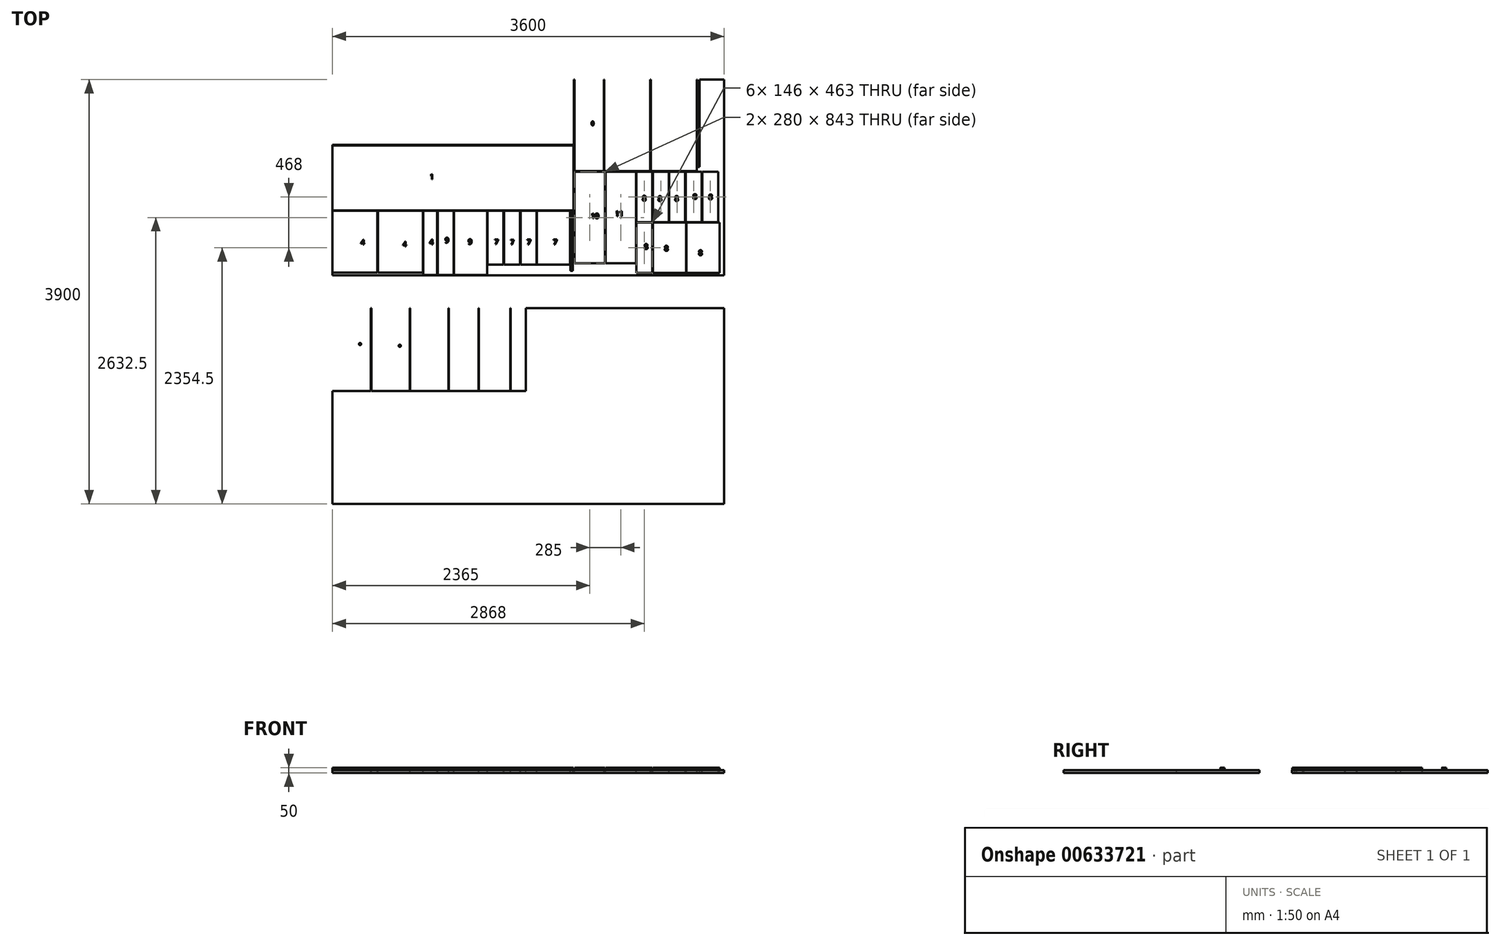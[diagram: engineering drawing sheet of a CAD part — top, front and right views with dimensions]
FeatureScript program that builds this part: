
annotation { "Feature Type Name" : "Feature", "Feature Type Description" : "" }
export const myFeature = defineFeature(function(context is Context, id is Id, definition is map)
    precondition{}
    {
        {
            var Q0;
            Q0=qCreatedBy(makeId("Top.planeOp"),FACE);
            var sketch = newSketch(context, id + "F0", { "sketchPlane" : qUnion([Q0])});
            skLineSegment(sketch, "E0.bottom", {"start": v(0, 0) * mm, "end": v(-3600, 0) * mm});
            skLineSegment(sketch, "E0.top", {"start": v(0, 1800) * mm, "end": v(-3600, 1800) * mm});
            skLineSegment(sketch, "E0.left", {"start": v(0, 0) * mm, "end": v(0, 1800) * mm});
            skLineSegment(sketch, "E0.right", {"start": v(-3600, 0) * mm, "end": v(-3600, 1800) * mm});
            skLineSegment(sketch, "E1.bottom", {"start": v(-3600, 1800) * mm, "end": v(-1380, 1800) * mm});
            skLineSegment(sketch, "E1.top", {"start": v(-3600, 1200) * mm, "end": v(-1380, 1200) * mm});
            skLineSegment(sketch, "E1.left", {"start": v(-3600, 1800) * mm, "end": v(-3600, 1200) * mm});
            skLineSegment(sketch, "E1.right", {"start": v(-1380, 1800) * mm, "end": v(-1380, 1200) * mm});
            skLineSegment(sketch, "E2.bottom", {"start": v(-3600, 1195) * mm, "end": v(-1384, 1195) * mm});
            skLineSegment(sketch, "E2.top", {"start": v(-3600, 599) * mm, "end": v(-1384, 599) * mm});
            skLineSegment(sketch, "E2.left", {"start": v(-3600, 1195) * mm, "end": v(-3600, 599) * mm});
            skLineSegment(sketch, "E2.right", {"start": v(-1384, 1195) * mm, "end": v(-1384, 599) * mm});
            skLineSegment(sketch, "E3.bottom", {"start": v(-3600, -300) * mm, "end": v(0, -300) * mm});
            skLineSegment(sketch, "E3.top", {"start": v(-3600, -2100) * mm, "end": v(0, -2100) * mm});
            skLineSegment(sketch, "E3.left", {"start": v(-3600, -300) * mm, "end": v(-3600, -2100) * mm});
            skLineSegment(sketch, "E3.right", {"start": v(0, -300) * mm, "end": v(0, -2100) * mm});
            skLineSegment(sketch, "E4.bottom", {"start": v(-3600, 594) * mm, "end": v(-3187, 594) * mm});
            skLineSegment(sketch, "E4.top", {"start": v(-3600, 28) * mm, "end": v(-3187, 28) * mm});
            skLineSegment(sketch, "E4.left", {"start": v(-3600, 594) * mm, "end": v(-3600, 28) * mm});
            skLineSegment(sketch, "E4.right", {"start": v(-3187, 594) * mm, "end": v(-3187, 28) * mm});
            skLineSegment(sketch, "E5.bottom", {"start": v(-3182, 594) * mm, "end": v(-2769, 594) * mm});
            skLineSegment(sketch, "E5.top", {"start": v(-3182, 28) * mm, "end": v(-2769, 28) * mm});
            skLineSegment(sketch, "E5.left", {"start": v(-3182, 594) * mm, "end": v(-3182, 28) * mm});
            skLineSegment(sketch, "E5.right", {"start": v(-2769, 594) * mm, "end": v(-2769, 28) * mm});
            skPoint(sketch, "E6", {"position": v(-3393.5, 28) * mm});
            skLineSegment(sketch, "E7.bottom", {"start": v(-2764, 594) * mm, "end": v(-2638, 594) * mm});
            skLineSegment(sketch, "E7.top", {"start": v(-2764, 3) * mm, "end": v(-2638, 3) * mm});
            skLineSegment(sketch, "E7.left", {"start": v(-2764, 594) * mm, "end": v(-2764, 3) * mm});
            skLineSegment(sketch, "E7.right", {"start": v(-2638, 594) * mm, "end": v(-2638, 3) * mm});
            skLineSegment(sketch, "E8.bottom", {"start": v(-2633, 594) * mm, "end": v(-2487, 594) * mm});
            skLineSegment(sketch, "E8.top", {"start": v(-2633, 3) * mm, "end": v(-2487, 3) * mm});
            skLineSegment(sketch, "E8.left", {"start": v(-2633, 594) * mm, "end": v(-2633, 3) * mm});
            skLineSegment(sketch, "E8.right", {"start": v(-2487, 594) * mm, "end": v(-2487, 3) * mm});
            skLineSegment(sketch, "E9.bottom", {"start": v(-2482, 594) * mm, "end": v(-2178, 594) * mm});
            skLineSegment(sketch, "E9.top", {"start": v(-2482, 3) * mm, "end": v(-2178, 3) * mm});
            skLineSegment(sketch, "E9.left", {"start": v(-2482, 594) * mm, "end": v(-2482, 3) * mm});
            skLineSegment(sketch, "E9.right", {"start": v(-2178, 594) * mm, "end": v(-2178, 3) * mm});
            skLineSegment(sketch, "E10.bottom", {"start": v(-2173, 594) * mm, "end": v(-2027, 594) * mm});
            skLineSegment(sketch, "E10.top", {"start": v(-2173, 99) * mm, "end": v(-2027, 99) * mm});
            skLineSegment(sketch, "E10.left", {"start": v(-2173, 594) * mm, "end": v(-2173, 99) * mm});
            skLineSegment(sketch, "E10.right", {"start": v(-2027, 594) * mm, "end": v(-2027, 99) * mm});
            skLineSegment(sketch, "E11.bottom", {"start": v(-2022, 594) * mm, "end": v(-1876, 594) * mm});
            skLineSegment(sketch, "E11.top", {"start": v(-2022, 99) * mm, "end": v(-1876, 99) * mm});
            skLineSegment(sketch, "E11.left", {"start": v(-2022, 594) * mm, "end": v(-2022, 99) * mm});
            skLineSegment(sketch, "E11.right", {"start": v(-1876, 594) * mm, "end": v(-1876, 99) * mm});
            skLineSegment(sketch, "E12.bottom", {"start": v(-1871, 594) * mm, "end": v(-1725, 594) * mm});
            skLineSegment(sketch, "E12.top", {"start": v(-1871, 99) * mm, "end": v(-1725, 99) * mm});
            skLineSegment(sketch, "E12.left", {"start": v(-1871, 594) * mm, "end": v(-1871, 99) * mm});
            skLineSegment(sketch, "E12.right", {"start": v(-1725, 594) * mm, "end": v(-1725, 99) * mm});
            skLineSegment(sketch, "E13", {"start": v(-1380, 1800) * mm, "end": v(-1380, 0) * mm, "construction": true});
            skLineSegment(sketch, "E14.bottom", {"start": v(-1720, 594) * mm, "end": v(-1416, 594) * mm});
            skLineSegment(sketch, "E14.top", {"start": v(-1720, 99) * mm, "end": v(-1416, 99) * mm});
            skLineSegment(sketch, "E14.left", {"start": v(-1720, 594) * mm, "end": v(-1720, 99) * mm});
            skLineSegment(sketch, "E14.right", {"start": v(-1416, 594) * mm, "end": v(-1416, 99) * mm});
            skText(sketch, "E15", { "text": "7", "fontName": "OpenSans-Regular.ttf"});
            skText(sketch, "E16", { "text": "7", "fontName": "OpenSans-Regular.ttf"});
            skText(sketch, "E17", { "text": "7", "fontName": "OpenSans-Regular.ttf"});
            skText(sketch, "E18", { "text": "7", "fontName": "OpenSans-Regular.ttf"});
            skText(sketch, "E19", { "text": "9", "fontName": "OpenSans-Regular.ttf"});
            skText(sketch, "E20", { "text": "9", "fontName": "OpenSans-Regular.ttf"});
            skText(sketch, "E21", { "text": "4", "fontName": "OpenSans-Regular.ttf"});
            skText(sketch, "E22", { "text": "4", "fontName": "OpenSans-Regular.ttf"});
            skText(sketch, "E23", { "text": "4", "fontName": "OpenSans-Regular.ttf"});
            skText(sketch, "E24", { "text": "1", "fontName": "OpenSans-Regular.ttf"});
            skText(sketch, "E25", { "text": "1", "fontName": "OpenSans-Regular.ttf"});
            skLineSegment(sketch, "E26.bottom", {"start": v(-3600, -300) * mm, "end": v(-3247.5, -300) * mm});
            skLineSegment(sketch, "E26.top", {"start": v(-3600, -1061) * mm, "end": v(-3247.5, -1061) * mm});
            skLineSegment(sketch, "E26.left", {"start": v(-3600, -300) * mm, "end": v(-3600, -1061) * mm});
            skLineSegment(sketch, "E26.right", {"start": v(-3247.5, -300) * mm, "end": v(-3247.5, -1061) * mm});
            skLineSegment(sketch, "E27.bottom", {"start": v(-3242.5, -300) * mm, "end": v(-2890, -300) * mm});
            skLineSegment(sketch, "E27.top", {"start": v(-3242.5, -1061) * mm, "end": v(-2890, -1061) * mm});
            skLineSegment(sketch, "E27.left", {"start": v(-3242.5, -300) * mm, "end": v(-3242.5, -1061) * mm});
            skLineSegment(sketch, "E27.right", {"start": v(-2890, -300) * mm, "end": v(-2890, -1061) * mm});
            skLineSegment(sketch, "E28.bottom", {"start": v(-2885, -300) * mm, "end": v(-2534, -300) * mm});
            skLineSegment(sketch, "E28.top", {"start": v(-2885, -1061) * mm, "end": v(-2534, -1061) * mm});
            skLineSegment(sketch, "E28.left", {"start": v(-2885, -300) * mm, "end": v(-2885, -1061) * mm});
            skLineSegment(sketch, "E28.right", {"start": v(-2534, -300) * mm, "end": v(-2534, -1061) * mm});
            skLineSegment(sketch, "E29.bottom", {"start": v(-2253, -300) * mm, "end": v(-1965, -300) * mm});
            skLineSegment(sketch, "E29.top", {"start": v(-2253, -1061) * mm, "end": v(-1965, -1061) * mm});
            skLineSegment(sketch, "E29.left", {"start": v(-2253, -300) * mm, "end": v(-2253, -1061) * mm});
            skLineSegment(sketch, "E29.right", {"start": v(-1965, -300) * mm, "end": v(-1965, -1061) * mm});
            skLineSegment(sketch, "E30.bottom", {"start": v(-2529, -300) * mm, "end": v(-2258, -300) * mm});
            skLineSegment(sketch, "E30.top", {"start": v(-2529, -1061) * mm, "end": v(-2258, -1061) * mm});
            skLineSegment(sketch, "E30.left", {"start": v(-2529, -300) * mm, "end": v(-2529, -1061) * mm});
            skLineSegment(sketch, "E30.right", {"start": v(-2258, -300) * mm, "end": v(-2258, -1061) * mm});
            skLineSegment(sketch, "E31.bottom", {"start": v(-1960, -300) * mm, "end": v(-1821, -300) * mm});
            skLineSegment(sketch, "E31.top", {"start": v(-1960, -1061) * mm, "end": v(-1821, -1061) * mm});
            skLineSegment(sketch, "E31.left", {"start": v(-1960, -300) * mm, "end": v(-1960, -1061) * mm});
            skLineSegment(sketch, "E31.right", {"start": v(-1821, -300) * mm, "end": v(-1821, -1061) * mm});
            skText(sketch, "E32", { "text": "6", "fontName": "OpenSans-Regular.ttf"});
            skText(sketch, "E33", { "text": "6", "fontName": "OpenSans-Regular.ttf"});
            skText(sketch, "E34", { "text": "5", "fontName": "OpenSans-Regular.ttf"});
            skText(sketch, "E35", { "text": "5", "fontName": "OpenSans-Regular.ttf"});
            skText(sketch, "E36", { "text": "7", "fontName": "OpenSans-Regular.ttf"});
            skText(sketch, "E37", { "text": "3", "fontName": "OpenSans-Regular.ttf"});
            skLineSegment(sketch, "E38.bottom", {"start": v(-1375, 954) * mm, "end": v(-1095, 954) * mm});
            skLineSegment(sketch, "E38.top", {"start": v(-1375, 111) * mm, "end": v(-1095, 111) * mm});
            skLineSegment(sketch, "E38.left", {"start": v(-1375, 954) * mm, "end": v(-1375, 111) * mm});
            skLineSegment(sketch, "E38.right", {"start": v(-1095, 954) * mm, "end": v(-1095, 111) * mm});
            skLineSegment(sketch, "E39.bottom", {"start": v(-673.5, 1800) * mm, "end": v(-251, 1800) * mm});
            skLineSegment(sketch, "E39.top", {"start": v(-673.5, 959) * mm, "end": v(-251, 959) * mm});
            skLineSegment(sketch, "E39.left", {"start": v(-673.5, 1800) * mm, "end": v(-673.5, 959) * mm});
            skLineSegment(sketch, "E39.right", {"start": v(-251, 1800) * mm, "end": v(-251, 959) * mm});
            skLineSegment(sketch, "E40.bottom", {"start": v(-1375, 1800) * mm, "end": v(-1106, 1800) * mm});
            skLineSegment(sketch, "E40.top", {"start": v(-1375, 959) * mm, "end": v(-1106, 959) * mm});
            skLineSegment(sketch, "E40.left", {"start": v(-1375, 1800) * mm, "end": v(-1375, 959) * mm});
            skLineSegment(sketch, "E40.right", {"start": v(-1106, 1800) * mm, "end": v(-1106, 959) * mm});
            skLineSegment(sketch, "E41.bottom", {"start": v(-1101, 1800) * mm, "end": v(-678.5, 1800) * mm});
            skLineSegment(sketch, "E41.top", {"start": v(-1101, 959) * mm, "end": v(-678.5, 959) * mm});
            skLineSegment(sketch, "E41.left", {"start": v(-1101, 1800) * mm, "end": v(-1101, 959) * mm});
            skLineSegment(sketch, "E41.right", {"start": v(-678.5, 1800) * mm, "end": v(-678.5, 959) * mm});
            skLineSegment(sketch, "E42.bottom", {"start": v(-246, 1800) * mm, "end": v(-226, 1800) * mm});
            skLineSegment(sketch, "E42.top", {"start": v(-246, 998) * mm, "end": v(-226, 998) * mm});
            skLineSegment(sketch, "E42.left", {"start": v(-246, 1800) * mm, "end": v(-246, 998) * mm});
            skLineSegment(sketch, "E42.right", {"start": v(-226, 1800) * mm, "end": v(-226, 998) * mm});
            skLineSegment(sketch, "E43", {"start": v(-1375, 959) * mm, "end": v(0, 959) * mm, "construction": true});
            skText(sketch, "E44", { "text": "10", "fontName": "OpenSans-Regular.ttf"});
            skText(sketch, "E45", { "text": "11", "fontName": "OpenSans-Regular.ttf"});
            skText(sketch, "E46", { "text": "11", "fontName": "OpenSans-Regular.ttf"});
            skText(sketch, "E47", { "text": "10", "fontName": "OpenSans-Regular.ttf"});
            skLineSegment(sketch, "E48.bottom", {"start": v(-1090, 954) * mm, "end": v(-810, 954) * mm});
            skLineSegment(sketch, "E48.top", {"start": v(-1090, 111) * mm, "end": v(-810, 111) * mm});
            skLineSegment(sketch, "E48.left", {"start": v(-1090, 954) * mm, "end": v(-1090, 111) * mm});
            skLineSegment(sketch, "E48.right", {"start": v(-810, 954) * mm, "end": v(-810, 111) * mm});
            skText(sketch, "E49", { "text": "11", "fontName": "OpenSans-Regular.ttf"});
            skLineSegment(sketch, "E50.bottom", {"start": v(-805, 954) * mm, "end": v(-659, 954) * mm});
            skLineSegment(sketch, "E50.top", {"start": v(-805, 491) * mm, "end": v(-659, 491) * mm});
            skLineSegment(sketch, "E50.left", {"start": v(-805, 954) * mm, "end": v(-805, 491) * mm});
            skLineSegment(sketch, "E50.right", {"start": v(-659, 954) * mm, "end": v(-659, 491) * mm});
            skLineSegment(sketch, "E51.bottom", {"start": v(-654, 954) * mm, "end": v(-508, 954) * mm});
            skLineSegment(sketch, "E51.top", {"start": v(-654, 491) * mm, "end": v(-508, 491) * mm});
            skLineSegment(sketch, "E51.left", {"start": v(-654, 954) * mm, "end": v(-654, 491) * mm});
            skLineSegment(sketch, "E51.right", {"start": v(-508, 954) * mm, "end": v(-508, 491) * mm});
            skLineSegment(sketch, "E52.bottom", {"start": v(-503, 954) * mm, "end": v(-357, 954) * mm});
            skLineSegment(sketch, "E52.top", {"start": v(-503, 491) * mm, "end": v(-357, 491) * mm});
            skLineSegment(sketch, "E52.left", {"start": v(-503, 954) * mm, "end": v(-503, 491) * mm});
            skLineSegment(sketch, "E52.right", {"start": v(-357, 954) * mm, "end": v(-357, 491) * mm});
            skLineSegment(sketch, "E53.bottom", {"start": v(-352, 954) * mm, "end": v(-206, 954) * mm});
            skLineSegment(sketch, "E53.top", {"start": v(-352, 491) * mm, "end": v(-206, 491) * mm});
            skLineSegment(sketch, "E53.left", {"start": v(-352, 954) * mm, "end": v(-352, 491) * mm});
            skLineSegment(sketch, "E53.right", {"start": v(-206, 954) * mm, "end": v(-206, 491) * mm});
            skLineSegment(sketch, "E54.bottom", {"start": v(-201, 954) * mm, "end": v(-55, 954) * mm});
            skLineSegment(sketch, "E54.top", {"start": v(-201, 491) * mm, "end": v(-55, 491) * mm});
            skLineSegment(sketch, "E54.left", {"start": v(-201, 954) * mm, "end": v(-201, 491) * mm});
            skLineSegment(sketch, "E54.right", {"start": v(-55, 954) * mm, "end": v(-55, 491) * mm});
            skLineSegment(sketch, "E55.bottom", {"start": v(-805, 486) * mm, "end": v(-659, 486) * mm});
            skLineSegment(sketch, "E55.top", {"start": v(-805, 23) * mm, "end": v(-659, 23) * mm});
            skLineSegment(sketch, "E55.left", {"start": v(-805, 486) * mm, "end": v(-805, 23) * mm});
            skLineSegment(sketch, "E55.right", {"start": v(-659, 486) * mm, "end": v(-659, 23) * mm});
            skLineSegment(sketch, "E56.bottom", {"start": v(-654, 486) * mm, "end": v(-350, 486) * mm});
            skLineSegment(sketch, "E56.top", {"start": v(-654, 23) * mm, "end": v(-350, 23) * mm});
            skLineSegment(sketch, "E56.left", {"start": v(-654, 486) * mm, "end": v(-654, 23) * mm});
            skLineSegment(sketch, "E56.right", {"start": v(-350, 486) * mm, "end": v(-350, 23) * mm});
            skLineSegment(sketch, "E57.bottom", {"start": v(-1411, 594) * mm, "end": v(-1391, 594) * mm});
            skLineSegment(sketch, "E57.top", {"start": v(-1411, 42) * mm, "end": v(-1391, 42) * mm});
            skLineSegment(sketch, "E57.left", {"start": v(-1411, 594) * mm, "end": v(-1411, 42) * mm});
            skLineSegment(sketch, "E57.right", {"start": v(-1391, 594) * mm, "end": v(-1391, 42) * mm});
            skText(sketch, "E58", { "text": "8", "fontName": "OpenSans-Regular.ttf"});
            skText(sketch, "E59", { "text": "8", "fontName": "OpenSans-Regular.ttf"});
            skText(sketch, "E60", { "text": "8", "fontName": "OpenSans-Regular.ttf"});
            skText(sketch, "E61", { "text": "8", "fontName": "OpenSans-Regular.ttf"});
            skText(sketch, "E62", { "text": "8", "fontName": "OpenSans-Regular.ttf"});
            skText(sketch, "E63", { "text": "8", "fontName": "OpenSans-Regular.ttf"});
            skText(sketch, "E64", { "text": "8", "fontName": "OpenSans-Regular.ttf"});
            skLineSegment(sketch, "E65.bottom", {"start": v(-345, 486) * mm, "end": v(-41, 486) * mm});
            skLineSegment(sketch, "E65.top", {"start": v(-345, 23) * mm, "end": v(-41, 23) * mm});
            skLineSegment(sketch, "E65.left", {"start": v(-345, 486) * mm, "end": v(-345, 23) * mm});
            skLineSegment(sketch, "E65.right", {"start": v(-41, 486) * mm, "end": v(-41, 23) * mm});
            skText(sketch, "E66", { "text": "8", "fontName": "OpenSans-Regular.ttf"});
            const initialGuessF0  = {"E15": [-2.10921, 0.2869, 1, 0, 0.04638], "E16": [-1.965, 0.28355, 1, 0, 0.04638], "E17": [-1.8111, 0.2845, 1, 0, 0.04638], "E18": [-1.5711, 0.2845, 1, 0, 0.04638], "E19": [-2.35296, 0.28738, 1, 0, 0.04638], "E20": [-2.56596, 0.3013, 1, 0, 0.04638], "E21": [-2.709, 0.2855, 1, 0, 0.04638], "E22": [-2.9545, 0.26558, 1, 0, 0.04638], "E23": [-3.34023, 0.2825, 1, 0, 0.04638], "E24": [-2.7, 1.47, 1, 0, 0.04638], "E25": [-2.70346, 0.885, 1, 0, 0.04638], "E32": [-3.3649, -0.6445, 1, 0, 0.04638], "E33": [-3.00034, -0.66125, 1, 0, 0.04638], "E34": [-2.6205, -0.674, 1, 0, 0.04638], "E35": [-2.326, -0.6861, 1, 0, 0.04638], "E36": [-1.90976, -0.67968, 1, 0, 0.04638], "E37": [-2.11362, -0.68108, 1, 0, 0.04638], "E44": [-1.26293, 1.37555, 1, 0, 0.04638], "E45": [-0.88838, 1.39262, 1, 0, 0.04638], "E46": [-0.4975, 1.35498, 1, 0, 0.04638], "E47": [-1.22373, 0.52433, 1, 0, 0.04638], "E49": [-1.0003, 0.54532, 1, 0, 0.04638], "E58": [-0.549, 0.22673, 1, 0, 0.04638], "E59": [-0.75213, 0.68705, 1, 0, 0.04638], "E60": [-0.60792, 0.6837, 1, 0, 0.04638], "E61": [-0.454, 0.68466, 1, 0, 0.04638], "E62": [-0.28651, 0.7023, 1, 0, 0.04638], "E63": [-0.1423, 0.69897, 1, 0, 0.04638], "E64": [-0.735, 0.24273, 1, 0, 0.04638], "E66": [-0.2351, 0.18613, 1, 0, 0.04638]};
            skSetInitialGuess(sketch, initialGuessF0);
            skSolve(sketch);
        }
        {
            var Q0;
            Q0=makeQuery(id+"F0.imprint","IMPRINT",FACE,{"disambiguationData":[TD([[makeQuery(id+"F0.imprint","IMPRINT",EDGE,{"derivedFrom":sQuery(id+"F0.wireOp",EDGE,"E4.bottom")}),-1.0]])]});
            var Q1;
            Q1=makeQuery(id+"F0.imprint","IMPRINT",FACE,{"disambiguationData":[TD([[makeQuery(id+"F0.imprint","IMPRINT",EDGE,{"derivedFrom":sQuery(id+"F0.wireOp",EDGE,"E5.bottom")}),-1.0]])]});
            var Q2;
            Q2=makeQuery(id+"F0.imprint","IMPRINT",FACE,{"disambiguationData":[TD([[makeQuery(id+"F0.imprint","IMPRINT",EDGE,{"derivedFrom":sQuery(id+"F0.wireOp",EDGE,"E7.bottom")}),-1.0]])]});
            var Q3;
            Q3=makeQuery(id+"F0.imprint","IMPRINT",FACE,{"disambiguationData":[TD([[makeQuery(id+"F0.imprint","IMPRINT",EDGE,{"derivedFrom":sQuery(id+"F0.wireOp",EDGE,"E8.bottom")}),-1.0]])]});
            var Q4;
            Q4=makeQuery(id+"F0.imprint","IMPRINT",FACE,{"disambiguationData":[TD([[makeQuery(id+"F0.imprint","IMPRINT",EDGE,{"derivedFrom":sQuery(id+"F0.wireOp",EDGE,"E9.bottom")}),-1.0]])]});
            var Q5;
            Q5=makeQuery(id+"F0.imprint","IMPRINT",FACE,{"disambiguationData":[TD([[makeQuery(id+"F0.imprint","IMPRINT",EDGE,{"derivedFrom":sQuery(id+"F0.wireOp",EDGE,"E10.bottom")}),-1.0]])]});
            var Q6;
            Q6=makeQuery(id+"F0.imprint","IMPRINT",FACE,{"disambiguationData":[TD([[makeQuery(id+"F0.imprint","IMPRINT",EDGE,{"derivedFrom":sQuery(id+"F0.wireOp",EDGE,"E11.bottom")}),-1.0]])]});
            var Q7;
            Q7=makeQuery(id+"F0.imprint","IMPRINT",FACE,{"disambiguationData":[TD([[makeQuery(id+"F0.imprint","IMPRINT",EDGE,{"derivedFrom":sQuery(id+"F0.wireOp",EDGE,"E12.bottom")}),-1.0]])]});
            var Q8;
            Q8=makeQuery(id+"F0.imprint","IMPRINT",FACE,{"disambiguationData":[TD([[makeQuery(id+"F0.imprint","IMPRINT",EDGE,{"derivedFrom":sQuery(id+"F0.wireOp",EDGE,"E14.bottom")}),-1.0]])]});
            var Q9;
            Q9=makeQuery(id+"F0.imprint","IMPRINT",FACE,{"disambiguationData":[TD([[makeQuery(id+"F0.imprint","IMPRINT",EDGE,{"derivedFrom":sQuery(id+"F0.wireOp",EDGE,"E57.bottom")}),-1.0]])]});
            var Q10;
            Q10=makeQuery(id+"F0.imprint","IMPRINT",FACE,{"disambiguationData":[TD([[makeQuery(id+"F0.imprint","IMPRINT",EDGE,{"derivedFrom":sQuery(id+"F0.wireOp",EDGE,"E38.bottom")}),-1.0]])]});
            var Q11;
            Q11=makeQuery(id+"F0.imprint","IMPRINT",FACE,{"disambiguationData":[TD([[makeQuery(id+"F0.imprint","IMPRINT",EDGE,{"derivedFrom":sQuery(id+"F0.wireOp",EDGE,"E47.sketch_text.stroke-17")}),1.0]])]});
            var Q12;
            Q12=makeQuery(id+"F0.imprint","IMPRINT",FACE,{"disambiguationData":[TD([[makeQuery(id+"F0.imprint","IMPRINT",EDGE,{"derivedFrom":sQuery(id+"F0.wireOp",EDGE,"E48.bottom")}),-1.0]])]});
            var Q13;
            Q13=makeQuery(id+"F0.imprint","IMPRINT",FACE,{"disambiguationData":[TD([[makeQuery(id+"F0.imprint","IMPRINT",EDGE,{"derivedFrom":sQuery(id+"F0.wireOp",EDGE,"E2.bottom")}),-1.0]])]});
            var Q14;
            Q14=makeQuery(id+"F0.imprint","IMPRINT",FACE,{"disambiguationData":[TD([[makeQuery(id+"F0.imprint","IMPRINT",EDGE,{"derivedFrom":sQuery(id+"F0.wireOp",EDGE,"E21.sketch_text.stroke-11")}),1.0]])]});
            var Q15;
            Q15=makeQuery(id+"F0.imprint","IMPRINT",FACE,{"disambiguationData":[TD([[makeQuery(id+"F0.imprint","IMPRINT",EDGE,{"derivedFrom":sQuery(id+"F0.wireOp",EDGE,"E20.sketch_text.stroke-16")}),1.0]])]});
            var Q16;
            Q16=makeQuery(id+"F0.imprint","IMPRINT",FACE,{"disambiguationData":[TD([[makeQuery(id+"F0.imprint","IMPRINT",EDGE,{"derivedFrom":sQuery(id+"F0.wireOp",EDGE,"E19.sketch_text.stroke-16")}),1.0]])]});
            var Q17;
            Q17=makeQuery(id+"F0.imprint","IMPRINT",FACE,{"disambiguationData":[TD([[makeQuery(id+"F0.imprint","IMPRINT",EDGE,{"derivedFrom":sQuery(id+"F0.wireOp",EDGE,"E22.sketch_text.stroke-11")}),1.0]])]});
            var Q18;
            Q18=makeQuery(id+"F0.imprint","IMPRINT",FACE,{"disambiguationData":[TD([[makeQuery(id+"F0.imprint","IMPRINT",EDGE,{"derivedFrom":sQuery(id+"F0.wireOp",EDGE,"E23.sketch_text.stroke-11")}),1.0]])]});
            var Q19;
            Q19=makeQuery(id+"F0.imprint","IMPRINT",FACE,{"disambiguationData":[TD([[makeQuery(id+"F0.imprint","IMPRINT",EDGE,{"derivedFrom":sQuery(id+"F0.wireOp",EDGE,"E55.bottom")}),-1.0]])]});
            var Q20;
            Q20=makeQuery(id+"F0.imprint","IMPRINT",FACE,{"disambiguationData":[TD([[makeQuery(id+"F0.imprint","IMPRINT",EDGE,{"derivedFrom":sQuery(id+"F0.wireOp",EDGE,"E64.sketch_text.stroke-15")}),1.0]])]});
            var Q21;
            Q21=makeQuery(id+"F0.imprint","IMPRINT",FACE,{"disambiguationData":[TD([[makeQuery(id+"F0.imprint","IMPRINT",EDGE,{"derivedFrom":sQuery(id+"F0.wireOp",EDGE,"E64.sketch_text.stroke-23")}),1.0]])]});
            var Q22;
            Q22=makeQuery(id+"F0.imprint","IMPRINT",FACE,{"disambiguationData":[TD([[makeQuery(id+"F0.imprint","IMPRINT",EDGE,{"derivedFrom":sQuery(id+"F0.wireOp",EDGE,"E56.bottom")}),-1.0]])]});
            var Q23;
            Q23=makeQuery(id+"F0.imprint","IMPRINT",FACE,{"disambiguationData":[TD([[makeQuery(id+"F0.imprint","IMPRINT",EDGE,{"derivedFrom":sQuery(id+"F0.wireOp",EDGE,"E58.sketch_text.stroke-15")}),1.0]])]});
            var Q24;
            Q24=makeQuery(id+"F0.imprint","IMPRINT",FACE,{"disambiguationData":[TD([[makeQuery(id+"F0.imprint","IMPRINT",EDGE,{"derivedFrom":sQuery(id+"F0.wireOp",EDGE,"E58.sketch_text.stroke-23")}),1.0]])]});
            var Q25;
            Q25=makeQuery(id+"F0.imprint","IMPRINT",FACE,{"disambiguationData":[TD([[makeQuery(id+"F0.imprint","IMPRINT",EDGE,{"derivedFrom":sQuery(id+"F0.wireOp",EDGE,"E65.bottom")}),-1.0]])]});
            var Q26;
            Q26=makeQuery(id+"F0.imprint","IMPRINT",FACE,{"disambiguationData":[TD([[makeQuery(id+"F0.imprint","IMPRINT",EDGE,{"derivedFrom":sQuery(id+"F0.wireOp",EDGE,"E66.sketch_text.stroke-15")}),1.0]])]});
            var Q27;
            Q27=makeQuery(id+"F0.imprint","IMPRINT",FACE,{"disambiguationData":[TD([[makeQuery(id+"F0.imprint","IMPRINT",EDGE,{"derivedFrom":sQuery(id+"F0.wireOp",EDGE,"E66.sketch_text.stroke-23")}),1.0]])]});
            var Q28;
            Q28=makeQuery(id+"F0.imprint","IMPRINT",FACE,{"disambiguationData":[TD([[makeQuery(id+"F0.imprint","IMPRINT",EDGE,{"derivedFrom":sQuery(id+"F0.wireOp",EDGE,"E54.bottom")}),-1.0]])]});
            var Q29;
            Q29=makeQuery(id+"F0.imprint","IMPRINT",FACE,{"disambiguationData":[TD([[makeQuery(id+"F0.imprint","IMPRINT",EDGE,{"derivedFrom":sQuery(id+"F0.wireOp",EDGE,"E53.bottom")}),-1.0]])]});
            var Q30;
            Q30=makeQuery(id+"F0.imprint","IMPRINT",FACE,{"disambiguationData":[TD([[makeQuery(id+"F0.imprint","IMPRINT",EDGE,{"derivedFrom":sQuery(id+"F0.wireOp",EDGE,"E52.bottom")}),-1.0]])]});
            var Q31;
            Q31=makeQuery(id+"F0.imprint","IMPRINT",FACE,{"disambiguationData":[TD([[makeQuery(id+"F0.imprint","IMPRINT",EDGE,{"derivedFrom":sQuery(id+"F0.wireOp",EDGE,"E51.bottom")}),-1.0]])]});
            var Q32;
            Q32=makeQuery(id+"F0.imprint","IMPRINT",FACE,{"disambiguationData":[TD([[makeQuery(id+"F0.imprint","IMPRINT",EDGE,{"derivedFrom":sQuery(id+"F0.wireOp",EDGE,"E50.bottom")}),-1.0]])]});
            var Q33;
            Q33=makeQuery(id+"F0.imprint","IMPRINT",FACE,{"disambiguationData":[TD([[makeQuery(id+"F0.imprint","IMPRINT",EDGE,{"derivedFrom":sQuery(id+"F0.wireOp",EDGE,"E59.sketch_text.stroke-23")}),1.0]])]});
            var Q34;
            Q34=makeQuery(id+"F0.imprint","IMPRINT",FACE,{"disambiguationData":[TD([[makeQuery(id+"F0.imprint","IMPRINT",EDGE,{"derivedFrom":sQuery(id+"F0.wireOp",EDGE,"E59.sketch_text.stroke-15")}),1.0]])]});
            var Q35;
            Q35=makeQuery(id+"F0.imprint","IMPRINT",FACE,{"disambiguationData":[TD([[makeQuery(id+"F0.imprint","IMPRINT",EDGE,{"derivedFrom":sQuery(id+"F0.wireOp",EDGE,"E60.sketch_text.stroke-15")}),1.0]])]});
            var Q36;
            Q36=makeQuery(id+"F0.imprint","IMPRINT",FACE,{"disambiguationData":[TD([[makeQuery(id+"F0.imprint","IMPRINT",EDGE,{"derivedFrom":sQuery(id+"F0.wireOp",EDGE,"E60.sketch_text.stroke-23")}),1.0]])]});
            var Q37;
            Q37=makeQuery(id+"F0.imprint","IMPRINT",FACE,{"disambiguationData":[TD([[makeQuery(id+"F0.imprint","IMPRINT",EDGE,{"derivedFrom":sQuery(id+"F0.wireOp",EDGE,"E61.sketch_text.stroke-15")}),1.0]])]});
            var Q38;
            Q38=makeQuery(id+"F0.imprint","IMPRINT",FACE,{"disambiguationData":[TD([[makeQuery(id+"F0.imprint","IMPRINT",EDGE,{"derivedFrom":sQuery(id+"F0.wireOp",EDGE,"E61.sketch_text.stroke-23")}),1.0]])]});
            var Q39;
            Q39=makeQuery(id+"F0.imprint","IMPRINT",FACE,{"disambiguationData":[TD([[makeQuery(id+"F0.imprint","IMPRINT",EDGE,{"derivedFrom":sQuery(id+"F0.wireOp",EDGE,"E62.sketch_text.stroke-15")}),1.0]])]});
            var Q40;
            Q40=makeQuery(id+"F0.imprint","IMPRINT",FACE,{"disambiguationData":[TD([[makeQuery(id+"F0.imprint","IMPRINT",EDGE,{"derivedFrom":sQuery(id+"F0.wireOp",EDGE,"E62.sketch_text.stroke-23")}),1.0]])]});
            var Q41;
            Q41=makeQuery(id+"F0.imprint","IMPRINT",FACE,{"disambiguationData":[TD([[makeQuery(id+"F0.imprint","IMPRINT",EDGE,{"derivedFrom":sQuery(id+"F0.wireOp",EDGE,"E63.sketch_text.stroke-15")}),1.0]])]});
            var Q42;
            Q42=makeQuery(id+"F0.imprint","IMPRINT",FACE,{"disambiguationData":[TD([[makeQuery(id+"F0.imprint","IMPRINT",EDGE,{"derivedFrom":sQuery(id+"F0.wireOp",EDGE,"E63.sketch_text.stroke-23")}),1.0]])]});
            var Q43;
            Q43=makeQuery(id+"F0.imprint","IMPRINT",FACE,{"disambiguationData":[TD([[makeQuery(id+"F0.imprint","IMPRINT",EDGE,{"derivedFrom":sQuery(id+"F0.wireOp",EDGE,"E40.bottom")}),-1.0]])]});
            var Q44;
            Q44=makeQuery(id+"F0.imprint","IMPRINT",FACE,{"disambiguationData":[TD([[makeQuery(id+"F0.imprint","IMPRINT",EDGE,{"derivedFrom":sQuery(id+"F0.wireOp",EDGE,"E41.bottom")}),-1.0]])]});
            var Q45;
            Q45=makeQuery(id+"F0.imprint","IMPRINT",FACE,{"disambiguationData":[TD([[makeQuery(id+"F0.imprint","IMPRINT",EDGE,{"derivedFrom":sQuery(id+"F0.wireOp",EDGE,"E1.bottom")}),-1.0]])]});
            var Q46;
            Q46=makeQuery(id+"F0.imprint","IMPRINT",FACE,{"disambiguationData":[TD([[makeQuery(id+"F0.imprint","IMPRINT",EDGE,{"derivedFrom":sQuery(id+"F0.wireOp",EDGE,"E39.bottom")}),-1.0]])]});
            var Q47;
            Q47=makeQuery(id+"F0.imprint","IMPRINT",FACE,{"disambiguationData":[TD([[makeQuery(id+"F0.imprint","IMPRINT",EDGE,{"derivedFrom":sQuery(id+"F0.wireOp",EDGE,"E42.bottom")}),-1.0]])]});
            var Q48;
            Q48=makeQuery(id+"F0.imprint","IMPRINT",FACE,{"disambiguationData":[TD([[makeQuery(id+"F0.imprint","IMPRINT",EDGE,{"derivedFrom":sQuery(id+"F0.wireOp",EDGE,"E44.sketch_text.stroke-17")}),1.0]])]});
            var Q49;
            Q49=makeQuery(id+"F0.imprint","IMPRINT",FACE,{"disambiguationData":[TD([[makeQuery(id+"F0.imprint","IMPRINT",EDGE,{"derivedFrom":sQuery(id+"F0.wireOp",EDGE,"E26.bottom")}),-1.0]])]});
            var Q50;
            Q50=makeQuery(id+"F0.imprint","IMPRINT",FACE,{"disambiguationData":[TD([[makeQuery(id+"F0.imprint","IMPRINT",EDGE,{"derivedFrom":sQuery(id+"F0.wireOp",EDGE,"E27.bottom")}),-1.0]])]});
            var Q51;
            Q51=makeQuery(id+"F0.imprint","IMPRINT",FACE,{"disambiguationData":[TD([[makeQuery(id+"F0.imprint","IMPRINT",EDGE,{"derivedFrom":sQuery(id+"F0.wireOp",EDGE,"E28.bottom")}),-1.0]])]});
            var Q52;
            Q52=makeQuery(id+"F0.imprint","IMPRINT",FACE,{"disambiguationData":[TD([[makeQuery(id+"F0.imprint","IMPRINT",EDGE,{"derivedFrom":sQuery(id+"F0.wireOp",EDGE,"E30.bottom")}),-1.0]])]});
            var Q53;
            Q53=makeQuery(id+"F0.imprint","IMPRINT",FACE,{"disambiguationData":[TD([[makeQuery(id+"F0.imprint","IMPRINT",EDGE,{"derivedFrom":sQuery(id+"F0.wireOp",EDGE,"E29.bottom")}),-1.0]])]});
            var Q54;
            Q54=makeQuery(id+"F0.imprint","IMPRINT",FACE,{"disambiguationData":[TD([[makeQuery(id+"F0.imprint","IMPRINT",EDGE,{"derivedFrom":sQuery(id+"F0.wireOp",EDGE,"E31.bottom")}),-1.0]])]});
            var Q55;
            Q55=makeQuery(id+"F0.imprint","IMPRINT",FACE,{"disambiguationData":[TD([[makeQuery(id+"F0.imprint","IMPRINT",EDGE,{"derivedFrom":sQuery(id+"F0.wireOp",EDGE,"E33.sketch_text.stroke-15")}),1.0]])]});
            var Q56;
            Q56=makeQuery(id+"F0.imprint","IMPRINT",FACE,{"disambiguationData":[TD([[makeQuery(id+"F0.imprint","IMPRINT",EDGE,{"derivedFrom":sQuery(id+"F0.wireOp",EDGE,"E32.sketch_text.stroke-15")}),1.0]])]});
            extrude(context, id + "F1", {"entities" : qUnion([Q0, Q1, Q2, Q3, Q4, Q5, Q6, Q7, Q8, Q9, Q10, Q11, Q12, Q13, Q14, Q15, Q16, Q17, Q18, Q19, Q20, Q21, Q22, Q23, Q24, Q25, Q26, Q27, Q28, Q29, Q30, Q31, Q32, Q33, Q34, Q35, Q36, Q37, Q38, Q39, Q40, Q41, Q42, Q43, Q44, Q45, Q46, Q47, Q48, Q49, Q50, Q51, Q52, Q53, Q54, Q55, Q56]), "depth" : 25 * mm, "offsetDistance" : 25 * mm});
        }
        {
            var Q0;
            {var subQ17=sQuery(id+"F0.wireOp",EDGE,"E0.bottom");Q0=makeQuery(id+"F0.imprint","IMPRINT",FACE,{"disambiguationData":[TD([[makeQuery(id+"F0.imprint","IMPRINT",EDGE,{"derivedFrom":subQ17}),-1.0]])]});}
            var Q1;
            Q1=makeQuery(id+"F0.imprint","IMPRINT",FACE,{"disambiguationData":[TD([[makeQuery(id+"F0.imprint","IMPRINT",EDGE,{"derivedFrom":sQuery(id+"F0.wireOp",EDGE,"E3.top")}),1.0]])]});
            extrude(context, id + "F2", {"entities" : qUnion([Q0, Q1]), "oppositeDirection" : true, "depth" : 25 * mm, "offsetDistance" : 25 * mm});
        }
    });
